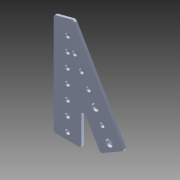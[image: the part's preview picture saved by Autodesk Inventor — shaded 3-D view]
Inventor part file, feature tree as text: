
AUTODESK INVENTOR PART (.ipt)
format: ipt  version: 2015 (Build 190159000, 159)  size: 158,208 bytes
history: native  units: in
note: dims shown in document units (in); Inventor stores cm internally (conversion verified against a paired STEP export)
features: other x2, extrude x1, imported_body x1, sketch x1, projected_geometry x1
ambient origin geometry x8: Origin, YZ Plane, XZ Plane, XY Plane, X Axis, Y Axis, Z Axis, Center Point
bodies: Body1 (feature_tree)
feature tree (6):
  other  "Cut-Extrude2"
  other  "Versaframe 30deg gusset1"
  extrude  "Extrusion1"  Depth=1.0in
  imported_body  "Base1"
  sketch  "Sketch1"  dims[d0=0.25in d1=0.25in d2=1.0in d3=0.0in]
  projected_geometry  "Projected Loop1"
